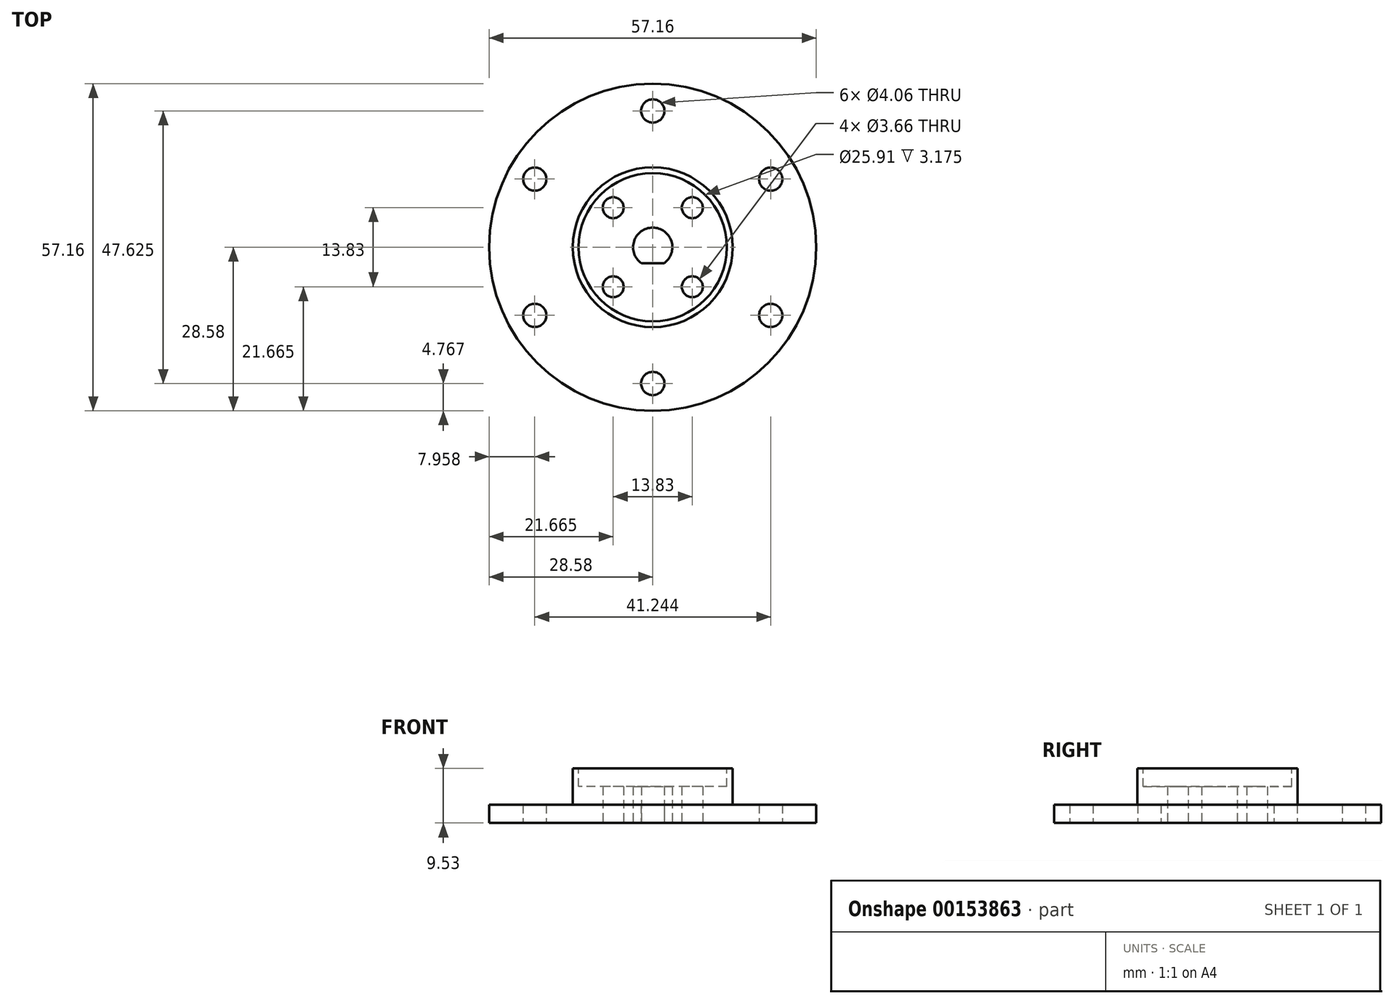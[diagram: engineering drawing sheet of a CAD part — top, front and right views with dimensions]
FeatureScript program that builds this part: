
annotation { "Feature Type Name" : "Feature", "Feature Type Description" : "" }
export const myFeature = defineFeature(function(context is Context, id is Id, definition is map)
    precondition{}
    {
        {
            var Q0;
            Q0=qCreatedBy(makeId("Top.planeOp"),FACE);
            var sketch = newSketch(context, id + "F0", { "sketchPlane" : qUnion([Q0])});
            skCircle(sketch, "E0", {"center": v(0, 0) * mm, "radius": 28.58 * mm});
            skPoint(sketch, "E1", {"position": v(0, 23.81) * mm});
            skCircle(sketch, "E2", {"center": v(0, 23.81) * mm, "radius": 2.03 * mm});
            skPoint(sketch, "E3.1.0", {"position": v(-20.62, -11.9) * mm});
            skPoint(sketch, "E3.2.0", {"position": v(20.62, -11.9) * mm});
            skCircle(sketch, "E4.1.0", {"center": v(-20.62, 11.9) * mm, "radius": 2.03 * mm});
            skCircle(sketch, "E4.2.0", {"center": v(-20.62, -11.9) * mm, "radius": 2.03 * mm});
            skCircle(sketch, "E4.3.0", {"center": v(0, -23.81) * mm, "radius": 2.03 * mm});
            skCircle(sketch, "E4.4.0", {"center": v(20.62, -11.9) * mm, "radius": 2.03 * mm});
            skCircle(sketch, "E4.5.0", {"center": v(20.62, 11.9) * mm, "radius": 2.03 * mm});
            skSolve(sketch);
        }
        {
            var Q0;
            Q0=makeQuery(id+"F0.imprint","IMPRINT",FACE,{"disambiguationData":[TD([[makeQuery(id+"F0.imprint","IMPRINT",EDGE,{"derivedFrom":sQuery(id+"F0.wireOp",EDGE,"E0")}),1.0]])]});
            extrude(context, id + "F1", {"entities" : qUnion([Q0]), "depth" : 3.17 * mm});
        }
        {
            var Q0;
            Q0=makeQuery(id+"F1.opExtrude","CAP_FACE",FACE,{"disambiguationData":[OSD([sQuery(id+"F0.wireOp",EDGE,"E0"),sQuery(id+"F0.wireOp",EDGE,"E2"),sQuery(id+"F0.wireOp",EDGE,"E4.1.0"),sQuery(id+"F0.wireOp",EDGE,"E4.2.0"),sQuery(id+"F0.wireOp",EDGE,"E4.3.0"),sQuery(id+"F0.wireOp",EDGE,"E4.4.0"),sQuery(id+"F0.wireOp",EDGE,"E4.5.0")])],"isStart":false});
            var sketch = newSketch(context, id + "F2", { "sketchPlane" : qUnion([Q0])});
            skCircle(sketch, "E5", {"center": v(0, 0) * mm, "radius": 13.97 * mm});
            skSolve(sketch);
        }
        {
            var Q0;
            Q0=makeQuery(id+"F2.imprint","IMPRINT",FACE,{"disambiguationData":[TD([[makeQuery(id+"F2.imprint","IMPRINT",EDGE,{"derivedFrom":sQuery(id+"F2.wireOp",EDGE,"E5")}),1.0]])]});
            extrude(context, id + "F3", {"entities" : qUnion([Q0]), "operationType" : NewBodyOperationType.ADD, "depth" : 6.35 * mm});
        }
        {
            var Q0;
            Q0=makeQuery(id+"F1.opExtrude","CAP_FACE",FACE,{"disambiguationData":[OSD([sQuery(id+"F0.wireOp",EDGE,"E0"),sQuery(id+"F0.wireOp",EDGE,"E2"),sQuery(id+"F0.wireOp",EDGE,"E4.1.0"),sQuery(id+"F0.wireOp",EDGE,"E4.2.0"),sQuery(id+"F0.wireOp",EDGE,"E4.3.0"),sQuery(id+"F0.wireOp",EDGE,"E4.4.0"),sQuery(id+"F0.wireOp",EDGE,"E4.5.0")])],"isStart":true});
            var sketch = newSketch(context, id + "F4", { "sketchPlane" : qUnion([Q0])});
            skCircle(sketch, "E6", {"center": v(0, 0) * mm, "radius": 3.43 * mm});
            skLineSegment(sketch, "E7", {"start": v(0, 2.8) * mm, "end": v(-1.99, 2.8) * mm});
            skLineSegment(sketch, "E8", {"start": v(-1.99, 2.8) * mm, "end": v(1.99, 2.8) * mm});
            skSolve(sketch);
        }
        {
            var Q0;
            {var subQ0=sQuery(id+"F4.wireOp",EDGE,"E8");var subQ4=makeQuery(id+"F4.imprint","IMPRINT",VERTEX,{"derivedFrom":subQ0});Q0=makeQuery(id+"F4.imprint","IMPRINT",FACE,{"disambiguationData":[TD([[makeQuery(id+"F4.imprint","IMPRINT",EDGE,{"disambiguationData":[TD([[subQ4,1.0]])],"derivedFrom":subQ0}),-1.0]])]});}
            extrude(context, id + "F5", {"entities" : qUnion([Q0]), "operationType" : NewBodyOperationType.REMOVE, "endBound" : BoundingType.UP_TO_NEXT, "oppositeDirection" : true, "depth" : 25.4 * mm});
        }
        {
            var Q0;
            Q0=makeQuery(id+"F1.opExtrude","CAP_FACE",FACE,{"disambiguationData":[OSD([sQuery(id+"F0.wireOp",EDGE,"E0"),sQuery(id+"F0.wireOp",EDGE,"E2"),sQuery(id+"F0.wireOp",EDGE,"E4.1.0"),sQuery(id+"F0.wireOp",EDGE,"E4.2.0"),sQuery(id+"F0.wireOp",EDGE,"E4.3.0"),sQuery(id+"F0.wireOp",EDGE,"E4.4.0"),sQuery(id+"F0.wireOp",EDGE,"E4.5.0")])],"isStart":true});
            var sketch = newSketch(context, id + "F6", { "sketchPlane" : qUnion([Q0])});
            skLineSegment(sketch, "E9.bottom", {"start": v(6.91, -6.91) * mm, "end": v(-6.91, -6.91) * mm});
            skLineSegment(sketch, "E9.top", {"start": v(6.91, 6.91) * mm, "end": v(-6.91, 6.91) * mm});
            skLineSegment(sketch, "E9.left", {"start": v(6.91, -6.91) * mm, "end": v(6.91, 6.91) * mm});
            skLineSegment(sketch, "E9.right", {"start": v(-6.91, -6.91) * mm, "end": v(-6.91, 6.91) * mm});
            skPoint(sketch, "E9.middle", {"position": v(0, 0) * mm});
            skCircle(sketch, "E10", {"center": v(-6.91, 6.91) * mm, "radius": 1.83 * mm});
            skCircle(sketch, "E11", {"center": v(6.91, 6.91) * mm, "radius": 1.83 * mm});
            skCircle(sketch, "E12", {"center": v(6.91, -6.91) * mm, "radius": 1.83 * mm});
            skCircle(sketch, "E13", {"center": v(-6.91, -6.91) * mm, "radius": 1.83 * mm});
            skSolve(sketch);
        }
        {
            var Q0;
            {var subQ0=sQuery(id+"F6.wireOp",EDGE,"E9.right");var subQ1=sQuery(id+"F6.wireOp",EDGE,"E9.bottom");var subQ2=makeQuery(id+"F6.imprint","INTERSECT",VERTEX,{"derivedFrom":[subQ1,subQ0]});Q0=makeQuery(id+"F6.imprint","IMPRINT",FACE,{"disambiguationData":[TD([[makeQuery(id+"F6.imprint","IMPRINT",EDGE,{"disambiguationData":[TD([[subQ2,1.0]])],"derivedFrom":subQ1}),-1.0]])]});}
            var Q1;
            {var subQ0=sQuery(id+"F6.wireOp",EDGE,"E9.right");var subQ1=sQuery(id+"F6.wireOp",EDGE,"E9.bottom");var subQ2=makeQuery(id+"F6.imprint","INTERSECT",VERTEX,{"derivedFrom":[subQ1,subQ0]});Q1=makeQuery(id+"F6.imprint","IMPRINT",FACE,{"disambiguationData":[TD([[makeQuery(id+"F6.imprint","IMPRINT",EDGE,{"disambiguationData":[TD([[subQ2,1.0]])],"derivedFrom":subQ1}),1.0]])]});}
            var Q2;
            {var subQ0=sQuery(id+"F6.wireOp",EDGE,"E9.right");var subQ1=sQuery(id+"F6.wireOp",EDGE,"E9.top");var subQ2=makeQuery(id+"F6.imprint","INTERSECT",VERTEX,{"derivedFrom":[subQ1,subQ0]});Q2=makeQuery(id+"F6.imprint","IMPRINT",FACE,{"disambiguationData":[TD([[makeQuery(id+"F6.imprint","IMPRINT",EDGE,{"disambiguationData":[TD([[subQ2,1.0]])],"derivedFrom":subQ1}),1.0]])]});}
            var Q3;
            {var subQ0=sQuery(id+"F6.wireOp",EDGE,"E9.right");var subQ1=sQuery(id+"F6.wireOp",EDGE,"E9.top");var subQ2=makeQuery(id+"F6.imprint","INTERSECT",VERTEX,{"derivedFrom":[subQ1,subQ0]});Q3=makeQuery(id+"F6.imprint","IMPRINT",FACE,{"disambiguationData":[TD([[makeQuery(id+"F6.imprint","IMPRINT",EDGE,{"disambiguationData":[TD([[subQ2,1.0]])],"derivedFrom":subQ1}),-1.0]])]});}
            var Q4;
            {var subQ0=sQuery(id+"F6.wireOp",EDGE,"E9.left");var subQ1=sQuery(id+"F6.wireOp",EDGE,"E9.top");var subQ2=makeQuery(id+"F6.imprint","INTERSECT",VERTEX,{"derivedFrom":[subQ1,subQ0]});Q4=makeQuery(id+"F6.imprint","IMPRINT",FACE,{"disambiguationData":[TD([[makeQuery(id+"F6.imprint","IMPRINT",EDGE,{"disambiguationData":[TD([[subQ2,-1.0]])],"derivedFrom":subQ1}),-1.0]])]});}
            var Q5;
            {var subQ0=sQuery(id+"F6.wireOp",EDGE,"E9.left");var subQ1=sQuery(id+"F6.wireOp",EDGE,"E9.top");var subQ2=makeQuery(id+"F6.imprint","INTERSECT",VERTEX,{"derivedFrom":[subQ1,subQ0]});Q5=makeQuery(id+"F6.imprint","IMPRINT",FACE,{"disambiguationData":[TD([[makeQuery(id+"F6.imprint","IMPRINT",EDGE,{"disambiguationData":[TD([[subQ2,-1.0]])],"derivedFrom":subQ1}),1.0]])]});}
            var Q6;
            {var subQ0=sQuery(id+"F6.wireOp",EDGE,"E9.left");var subQ1=sQuery(id+"F6.wireOp",EDGE,"E9.bottom");var subQ2=makeQuery(id+"F6.imprint","INTERSECT",VERTEX,{"derivedFrom":[subQ1,subQ0]});Q6=makeQuery(id+"F6.imprint","IMPRINT",FACE,{"disambiguationData":[TD([[makeQuery(id+"F6.imprint","IMPRINT",EDGE,{"disambiguationData":[TD([[subQ2,-1.0]])],"derivedFrom":subQ1}),-1.0]])]});}
            var Q7;
            {var subQ0=sQuery(id+"F6.wireOp",EDGE,"E9.left");var subQ1=sQuery(id+"F6.wireOp",EDGE,"E9.bottom");var subQ2=makeQuery(id+"F6.imprint","INTERSECT",VERTEX,{"derivedFrom":[subQ1,subQ0]});Q7=makeQuery(id+"F6.imprint","IMPRINT",FACE,{"disambiguationData":[TD([[makeQuery(id+"F6.imprint","IMPRINT",EDGE,{"disambiguationData":[TD([[subQ2,-1.0]])],"derivedFrom":subQ1}),1.0]])]});}
            var Q8;
            Q8=sQuery(id+"F6.wireOp",EDGE,"E12");
            var Q9;
            Q9=sQuery(id+"F6.wireOp",EDGE,"E11");
            var Q10;
            Q10=sQuery(id+"F6.wireOp",EDGE,"E10");
            var Q11;
            Q11=sQuery(id+"F6.wireOp",EDGE,"E13");
            extrude(context, id + "F7", {"entities" : qUnion([Q0, Q1, Q2, Q3, Q4, Q5, Q6, Q7]), "operationType" : NewBodyOperationType.REMOVE, "surfaceEntities" : qUnion([Q8, Q9, Q10, Q11]), "endBound" : BoundingType.UP_TO_NEXT, "oppositeDirection" : true, "depth" : 25.4 * mm});
        }
        {
            var Q0;
            Q0=makeQuery(id+"F3.opExtrude","CAP_FACE",FACE,{"disambiguationData":[OSD([sQuery(id+"F2.wireOp",EDGE,"E5")])],"isStart":false});
            var sketch = newSketch(context, id + "F8", { "sketchPlane" : qUnion([Q0])});
            skCircle(sketch, "E14", {"center": v(0, 0) * mm, "radius": 12.95 * mm});
            skSolve(sketch);
        }
        {
            var Q0;
            Q0=makeQuery(id+"F8.imprint","IMPRINT",FACE,{"disambiguationData":[TD([[makeQuery(id+"F8.imprint","IMPRINT",EDGE,{"derivedFrom":sQuery(id+"F8.wireOp",EDGE,"E14")}),1.0]])]});
            extrude(context, id + "F9", {"entities" : qUnion([Q0]), "operationType" : NewBodyOperationType.REMOVE, "oppositeDirection" : true, "depth" : 3.17 * mm});
        }
    });
